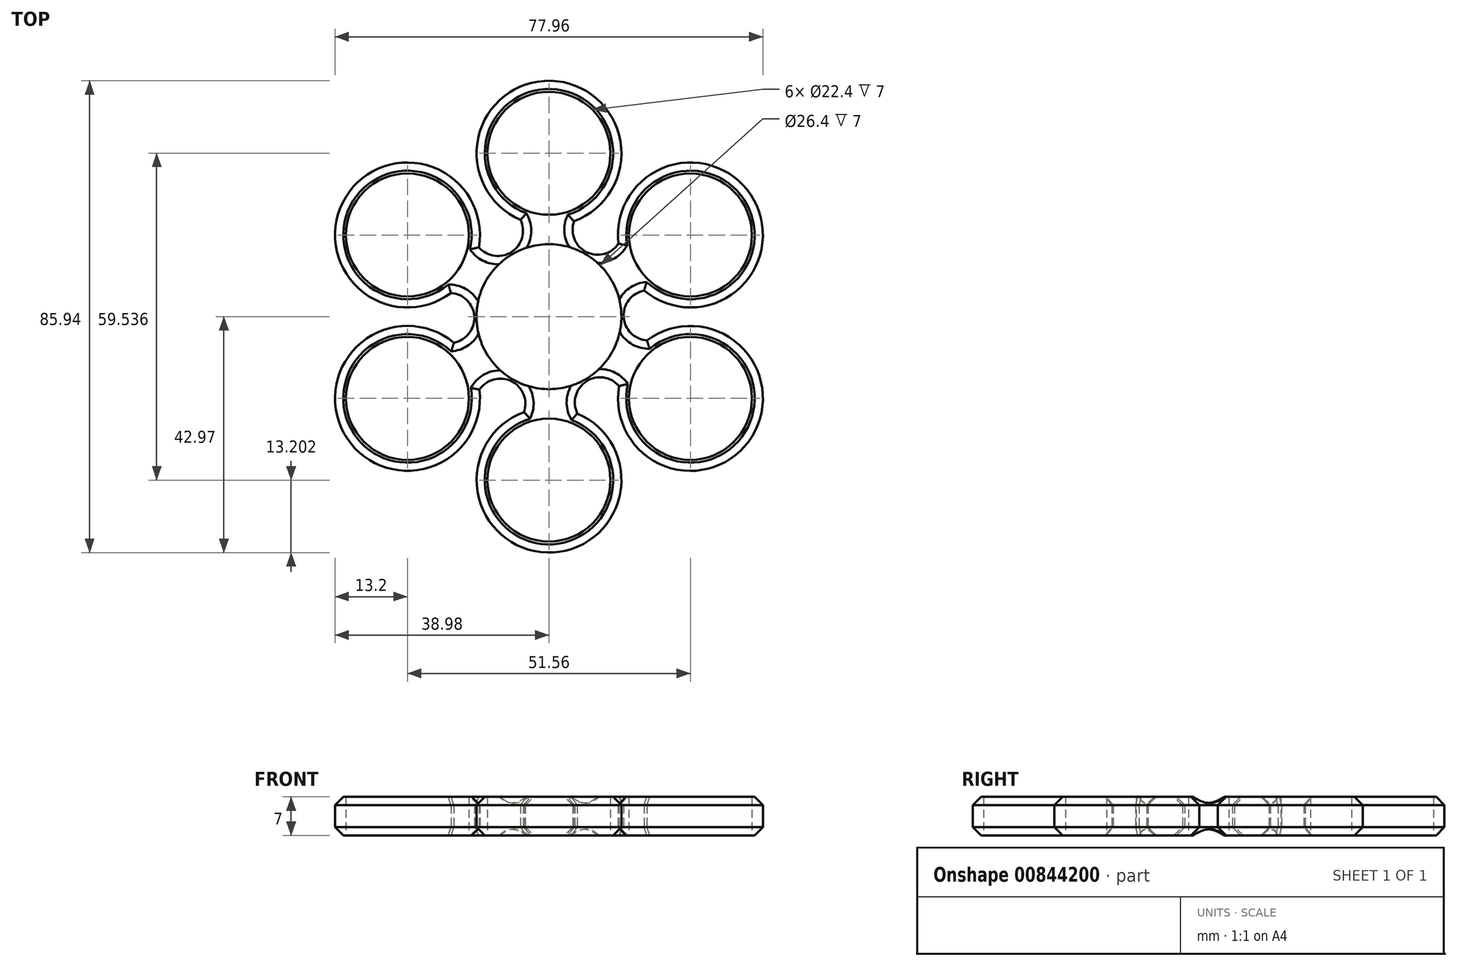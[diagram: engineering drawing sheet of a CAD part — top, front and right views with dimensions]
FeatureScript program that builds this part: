
annotation { "Feature Type Name" : "Feature", "Feature Type Description" : "" }
export const myFeature = defineFeature(function(context is Context, id is Id, definition is map)
    precondition{}
    {
        {
            var Q0;
            Q0=qCreatedBy(makeId("Top.planeOp"),FACE);
            var sketch = newSketch(context, id + "F0", { "sketchPlane" : qUnion([Q0])});
            skCircle(sketch, "E0", {"center": v(0, 0) * mm, "radius": 11.2 * mm});
            skCircle(sketch, "E1", {"center": v(0, 0) * mm, "radius": 13.2 * mm});
            skCircle(sketch, "E2", {"center": v(0, 29.77) * mm, "radius": 11.2 * mm});
            skArc(sketch, "E3", {"start": v(4.56, 17.38) * mm, "mid": v(0.33, 42.96) * mm, "end": v(-5.18, 17.63) * mm});
            skCircle(sketch, "E4.1.0", {"center": v(-25.78, 14.88) * mm, "radius": 11.2 * mm});
            skArc(sketch, "E4.1.1", {"start": v(-12.77, 12.64) * mm, "mid": v(-37.04, 21.77) * mm, "end": v(-17.86, 4.33) * mm});
            skCircle(sketch, "E4.2.0", {"center": v(-25.78, -14.88) * mm, "radius": 11.2 * mm});
            skArc(sketch, "E4.2.1", {"start": v(-17.33, -4.74) * mm, "mid": v(-37.37, -21.2) * mm, "end": v(-12.67, -13.3) * mm});
            skCircle(sketch, "E4.3.0", {"center": v(0, -29.77) * mm, "radius": 11.2 * mm});
            skArc(sketch, "E4.3.1", {"start": v(-4.56, -17.38) * mm, "mid": v(-0.33, -42.96) * mm, "end": v(5.18, -17.63) * mm});
            skCircle(sketch, "E4.4.0", {"center": v(25.78, -14.88) * mm, "radius": 11.2 * mm});
            skArc(sketch, "E4.4.1", {"start": v(12.77, -12.64) * mm, "mid": v(37.04, -21.77) * mm, "end": v(17.86, -4.33) * mm});
            skCircle(sketch, "E4.5.0", {"center": v(25.78, 14.88) * mm, "radius": 11.2 * mm});
            skArc(sketch, "E4.5.1", {"start": v(17.33, 4.74) * mm, "mid": v(37.37, 21.2) * mm, "end": v(12.67, 13.3) * mm});
            skArc(sketch, "E5", {"start": v(-12.77, 12.64) * mm, "mid": v(-6.78, 11.8) * mm, "end": v(-5.18, 17.63) * mm});
            skArc(sketch, "E6.1.0", {"start": v(-17.33, -4.74) * mm, "mid": v(-13.6, 0.02) * mm, "end": v(-17.86, 4.33) * mm});
            skArc(sketch, "E6.2.0", {"start": v(-4.56, -17.38) * mm, "mid": v(-6.82, -11.77) * mm, "end": v(-12.67, -13.3) * mm});
            skArc(sketch, "E6.3.0", {"start": v(12.77, -12.64) * mm, "mid": v(6.78, -11.8) * mm, "end": v(5.18, -17.63) * mm});
            skArc(sketch, "E6.4.0", {"start": v(17.33, 4.74) * mm, "mid": v(13.6, -0.02) * mm, "end": v(17.86, -4.33) * mm});
            skArc(sketch, "E6.5.0", {"start": v(4.56, 17.38) * mm, "mid": v(6.82, 11.77) * mm, "end": v(12.67, 13.3) * mm});
            skSolve(sketch);
        }
        {
            var Q0;
            Q0=makeQuery(id+"F0.imprint","IMPRINT",FACE,{"disambiguationData":[TD([[makeQuery(id+"F0.imprint","IMPRINT",EDGE,{"derivedFrom":sQuery(id+"F0.wireOp",EDGE,"E1")}),-1.0]])]});
            extrude(context, id + "F1", {"entities" : qUnion([Q0]), "depth" : 7 * mm, "offsetDistance" : 25 * mm});
        }
        {
            var Q0;
            Q0=makeQuery(id+"F1.opExtrude","CAP_EDGE",EDGE,{"disambiguationData":[OSD([sQuery(id+"F0.wireOp",EDGE,"E4.3.1")])],"isStart":true});
            var Q1;
            Q1=makeQuery(id+"F1.opExtrude","CAP_EDGE",EDGE,{"disambiguationData":[OSD([sQuery(id+"F0.wireOp",EDGE,"E4.4.1")])],"isStart":true});
            var Q2;
            Q2=makeQuery(id+"F1.opExtrude","CAP_EDGE",EDGE,{"disambiguationData":[OSD([sQuery(id+"F0.wireOp",EDGE,"E6.3.0")])],"isStart":true});
            var Q3;
            Q3=makeQuery(id+"F1.opExtrude","CAP_EDGE",EDGE,{"disambiguationData":[OSD([sQuery(id+"F0.wireOp",EDGE,"E6.4.0")])],"isStart":true});
            var Q4;
            Q4=makeQuery(id+"F1.opExtrude","CAP_EDGE",EDGE,{"disambiguationData":[OSD([sQuery(id+"F0.wireOp",EDGE,"E6.2.0")])],"isStart":true});
            var Q5;
            Q5=makeQuery(id+"F1.opExtrude","CAP_EDGE",EDGE,{"disambiguationData":[OSD([sQuery(id+"F0.wireOp",EDGE,"E4.2.1")])],"isStart":true});
            var Q6;
            Q6=makeQuery(id+"F1.opExtrude","CAP_EDGE",EDGE,{"disambiguationData":[OSD([sQuery(id+"F0.wireOp",EDGE,"E6.1.0")])],"isStart":true});
            var Q7;
            Q7=makeQuery(id+"F1.opExtrude","CAP_EDGE",EDGE,{"disambiguationData":[OSD([sQuery(id+"F0.wireOp",EDGE,"E4.1.1")])],"isStart":true});
            var Q8;
            Q8=makeQuery(id+"F1.opExtrude","CAP_EDGE",EDGE,{"disambiguationData":[OSD([sQuery(id+"F0.wireOp",EDGE,"E5")])],"isStart":true});
            var Q9;
            Q9=makeQuery(id+"F1.opExtrude","CAP_EDGE",EDGE,{"disambiguationData":[OSD([sQuery(id+"F0.wireOp",EDGE,"E3")])],"isStart":true});
            var Q10;
            Q10=makeQuery(id+"F1.opExtrude","CAP_EDGE",EDGE,{"disambiguationData":[OSD([sQuery(id+"F0.wireOp",EDGE,"E6.5.0")])],"isStart":true});
            var Q11;
            Q11=makeQuery(id+"F1.opExtrude","CAP_EDGE",EDGE,{"disambiguationData":[OSD([sQuery(id+"F0.wireOp",EDGE,"E4.5.1")])],"isStart":true});
            chamfer(context, id + "F2", {"entities" : qUnion([Q0, Q1, Q2, Q3, Q4, Q5, Q6, Q7, Q8, Q9, Q10, Q11]), "width" : 1.5 * mm, "tangentPropagation" : true});
        }
        {
            var Q0;
            Q0=makeQuery(id+"F1.opExtrude","CAP_EDGE",EDGE,{"disambiguationData":[OSD([sQuery(id+"F0.wireOp",EDGE,"E4.1.1")])],"isStart":false});
            var Q1;
            Q1=makeQuery(id+"F1.opExtrude","CAP_EDGE",EDGE,{"disambiguationData":[OSD([sQuery(id+"F0.wireOp",EDGE,"E3")])],"isStart":false});
            var Q2;
            Q2=makeQuery(id+"F1.opExtrude","CAP_EDGE",EDGE,{"disambiguationData":[OSD([sQuery(id+"F0.wireOp",EDGE,"E4.5.1")])],"isStart":false});
            var Q3;
            Q3=makeQuery(id+"F1.opExtrude","CAP_EDGE",EDGE,{"disambiguationData":[OSD([sQuery(id+"F0.wireOp",EDGE,"E4.4.1")])],"isStart":false});
            var Q4;
            Q4=makeQuery(id+"F1.opExtrude","CAP_EDGE",EDGE,{"disambiguationData":[OSD([sQuery(id+"F0.wireOp",EDGE,"E4.3.1")])],"isStart":false});
            var Q5;
            Q5=makeQuery(id+"F1.opExtrude","CAP_EDGE",EDGE,{"disambiguationData":[OSD([sQuery(id+"F0.wireOp",EDGE,"E4.2.1")])],"isStart":false});
            var Q6;
            Q6=makeQuery(id+"F1.opExtrude","CAP_EDGE",EDGE,{"disambiguationData":[OSD([sQuery(id+"F0.wireOp",EDGE,"E6.2.0")])],"isStart":false});
            var Q7;
            Q7=makeQuery(id+"F1.opExtrude","CAP_EDGE",EDGE,{"disambiguationData":[OSD([sQuery(id+"F0.wireOp",EDGE,"E6.1.0")])],"isStart":false});
            var Q8;
            Q8=makeQuery(id+"F1.opExtrude","CAP_EDGE",EDGE,{"disambiguationData":[OSD([sQuery(id+"F0.wireOp",EDGE,"E6.5.0")])],"isStart":false});
            var Q9;
            Q9=makeQuery(id+"F1.opExtrude","CAP_EDGE",EDGE,{"disambiguationData":[OSD([sQuery(id+"F0.wireOp",EDGE,"E5")])],"isStart":false});
            var Q10;
            Q10=makeQuery(id+"F1.opExtrude","CAP_EDGE",EDGE,{"disambiguationData":[OSD([sQuery(id+"F0.wireOp",EDGE,"E6.4.0")])],"isStart":false});
            var Q11;
            Q11=makeQuery(id+"F1.opExtrude","CAP_EDGE",EDGE,{"disambiguationData":[OSD([sQuery(id+"F0.wireOp",EDGE,"E6.3.0")])],"isStart":false});
            chamfer(context, id + "F3", {"entities" : qUnion([Q0, Q1, Q2, Q3, Q4, Q5, Q6, Q7, Q8, Q9, Q10, Q11]), "width" : 1.5 * mm, "tangentPropagation" : true});
        }
    });
